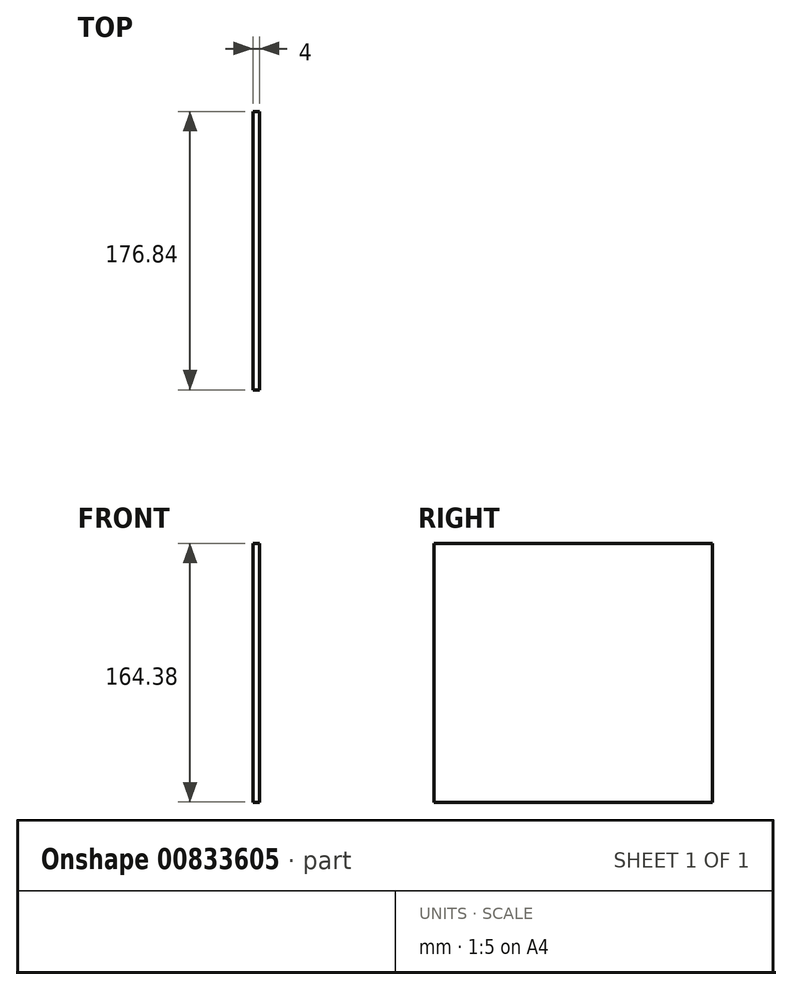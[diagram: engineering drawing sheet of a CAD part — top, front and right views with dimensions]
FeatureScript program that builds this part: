
annotation { "Feature Type Name" : "Feature", "Feature Type Description" : "" }
export const myFeature = defineFeature(function(context is Context, id is Id, definition is map)
    precondition{}
    {
        {
            var Q0;
            Q0=qCreatedBy(makeId("Right.planeOp"),FACE);
            var sketch = newSketch(context, id + "F0", { "sketchPlane" : qUnion([Q0])});
            skLineSegment(sketch, "E0.bottom", {"start": v(-85.8, 82.2) * mm, "end": v(91.04, 82.2) * mm});
            skLineSegment(sketch, "E0.top", {"start": v(-85.8, -82.2) * mm, "end": v(91.04, -82.2) * mm});
            skLineSegment(sketch, "E0.left", {"start": v(-85.8, 82.2) * mm, "end": v(-85.8, -82.2) * mm});
            skLineSegment(sketch, "E0.right", {"start": v(91.04, 82.2) * mm, "end": v(91.04, -82.2) * mm});
            skPoint(sketch, "E0.middle", {"position": v(2.62, 0) * mm});
            skPoint(sketch, "E1", {"position": v(0, -38.32) * mm});
            skLineSegment(sketch, "E2", {"start": v(0, 0) * mm, "end": v(0, -38.32) * mm});
            skSolve(sketch);
        }
        {
            var Q0;
            Q0 = qSketchRegion(id + "F0", true);
            extrude(context, id + "F1", {"entities" : qUnion([Q0]), "depth" : 2 * mm, "offsetDistance" : 25 * mm, "hasSecondDirection" : true, "secondDirectionOppositeDirection" : true, "secondDirectionDepth" : 2 * mm});
        }
        {
            var Q0;
            Q0=qCreatedBy(makeId("Front.planeOp"),FACE);
            var sketch = newSketch(context, id + "F2", { "sketchPlane" : qUnion([Q0])});
            skLineSegment(sketch, "E3", {"start": v(0, 0) * mm, "end": v(-50, 0) * mm});
            skSolve(sketch);
        }
        {
            var Q0;
            Q0=sQuery(id+"F2.wireOp",EDGE,"E3");
            extrude(context, id + "F3", {"bodyType" : ToolBodyType.SURFACE, "surfaceEntities" : qUnion([Q0]), "depth" : 25 * mm, "offsetDistance" : 25 * mm, "hasSecondDirection" : true, "secondDirectionOppositeDirection" : true, "secondDirectionDepth" : 25 * mm});
        }
        {
            var Q0;
            Q0=sQuery(id+"F0.wireOp",EDGE,"E2");
            extrude(context, id + "F4", {"bodyType" : ToolBodyType.SURFACE, "surfaceEntities" : qUnion([Q0]), "oppositeDirection" : true, "depth" : 49.7 * mm, "offsetDistance" : 25 * mm});
        }
    });
